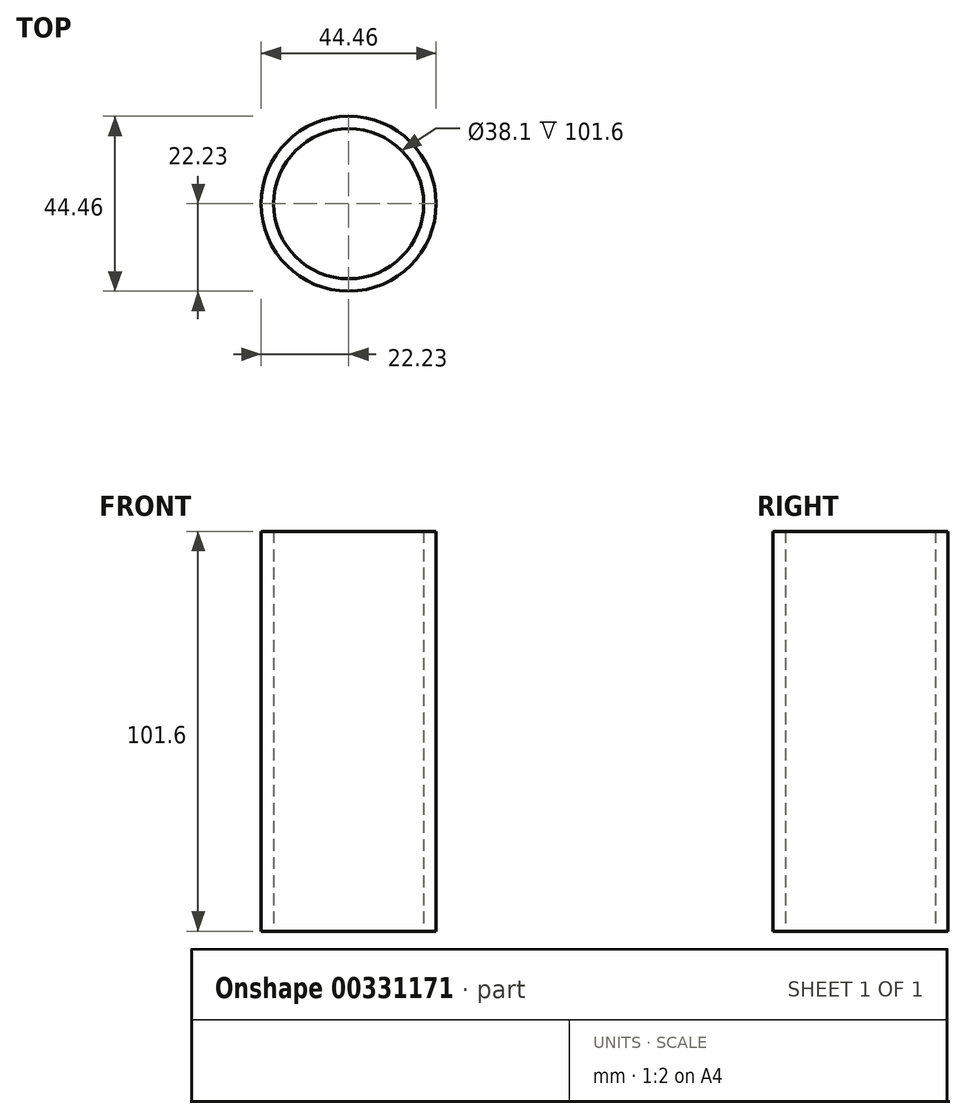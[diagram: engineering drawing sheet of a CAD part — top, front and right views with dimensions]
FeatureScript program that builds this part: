
annotation { "Feature Type Name" : "Feature", "Feature Type Description" : "" }
export const myFeature = defineFeature(function(context is Context, id is Id, definition is map)
    precondition{}
    {
        {
            var Q0;
            Q0=qCreatedBy(makeId("Top.planeOp"),FACE);
            var sketch = newSketch(context, id + "F0", { "sketchPlane" : qUnion([Q0])});
            skCircle(sketch, "E0", {"center": v(0, 0) * mm, "radius": 22.23 * mm});
            skCircle(sketch, "E1.0", {"center": v(0, 0) * mm, "radius": 19.05 * mm});
            skSolve(sketch);
        }
        {
            var Q0;
            Q0 = qSketchRegion(id + "F0", true);
            extrude(context, id + "F1", {"entities" : qUnion([Q0]), "depth" : 101.6 * mm});
        }
    });
